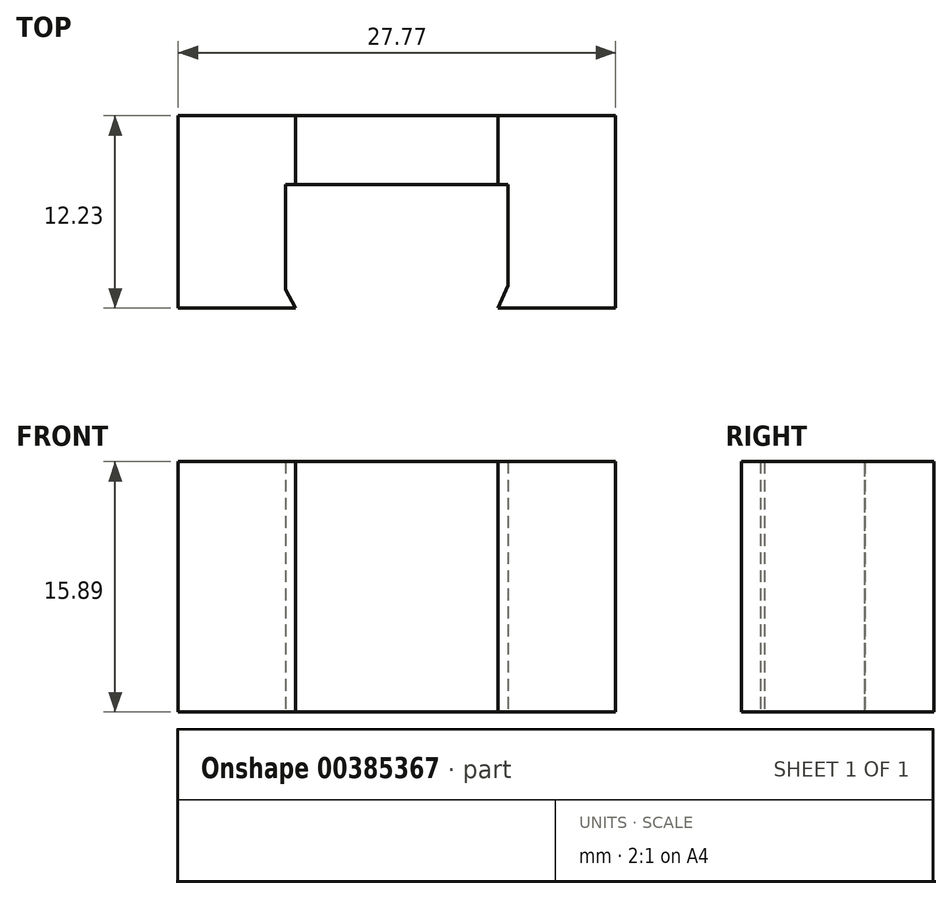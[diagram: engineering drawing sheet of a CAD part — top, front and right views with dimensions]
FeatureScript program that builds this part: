
annotation { "Feature Type Name" : "Feature", "Feature Type Description" : "" }
export const myFeature = defineFeature(function(context is Context, id is Id, definition is map)
    precondition{}
    {
        {
            var Q0;
            Q0=qCreatedBy(makeId("Front.planeOp"),FACE);
            var sketch = newSketch(context, id + "F0", { "sketchPlane" : qUnion([Q0])});
            skLineSegment(sketch, "E0", {"start": v(0, 0) * mm, "end": v(-27.77, 0) * mm});
            skLineSegment(sketch, "E1", {"start": v(-27.77, 0) * mm, "end": v(-27.77, -15.9) * mm});
            skLineSegment(sketch, "E2", {"start": v(-27.77, -15.9) * mm, "end": v(0, -15.9) * mm});
            skLineSegment(sketch, "E3", {"start": v(0, -15.9) * mm, "end": v(0, 0) * mm});
            skLineSegment(sketch, "E4", {"start": v(-20.32, 0) * mm, "end": v(-20.32, -15.9) * mm});
            skLineSegment(sketch, "E5", {"start": v(-20.32, -15.9) * mm, "end": v(-20.32, -11.79) * mm});
            skLineSegment(sketch, "E6", {"start": v(-7.45, -15.9) * mm, "end": v(-7.45, 0) * mm});
            skSolve(sketch);
        }
        {
            var Q0;
            {var subQ0=sQuery(id+"F0.wireOp",EDGE,"E3");Q0=makeQuery(id+"F0.imprint","IMPRINT",FACE,{"disambiguationData":[TD([[makeQuery(id+"F0.imprint","IMPRINT",EDGE,{"derivedFrom":subQ0}),1.0]])]});}
            var Q1;
            {var subQ1=sQuery(id+"F0.wireOp",EDGE,"E1");Q1=makeQuery(id+"F0.imprint","IMPRINT",FACE,{"disambiguationData":[TD([[makeQuery(id+"F0.imprint","IMPRINT",EDGE,{"derivedFrom":subQ1}),1.0]])]});}
            extrude(context, id + "F1", {"entities" : qUnion([Q0, Q1]), "depth" : 12.23 * mm});
        }
        {
            var Q0;
            {var subQ1=sQuery(id+"F0.wireOp",EDGE,"E4");Q0=makeQuery(id+"F0.imprint","IMPRINT",FACE,{"disambiguationData":[TD([[makeQuery(id+"F0.imprint","IMPRINT",EDGE,{"derivedFrom":subQ1}),1.0]])]});}
            extrude(context, id + "F2", {"entities" : qUnion([Q0]), "depth" : 4.39 * mm});
        }
        {
            var Q0;
            {var subQ0=sQuery(id+"F0.wireOp",EDGE,"E2");Q0=makeQuery(id+"F1.opExtrude","SWEPT_FACE",FACE,{"disambiguationData":[OSD([subQ0]),TDD([makeQuery(id+"F0.imprint","IMPRINT",EDGE,{"disambiguationData":[TD([[makeQuery(id+"F0.imprint","INTERSECT",VERTEX,{"derivedFrom":[subQ0,sQuery(id+"F0.wireOp",EDGE,"E3")]}),1.0]])],"derivedFrom":subQ0})])]});}
            var sketch = newSketch(context, id + "F3", { "sketchPlane" : qUnion([Q0])});
            skLineSegment(sketch, "E7", {"start": v(-7.45, 12.23) * mm, "end": v(-6.83, 10.78) * mm});
            skLineSegment(sketch, "E8", {"start": v(-6.83, 10.78) * mm, "end": v(-6.83, 4.42) * mm});
            skLineSegment(sketch, "E9", {"start": v(-6.83, 4.42) * mm, "end": v(-7.45, 4.42) * mm});
            skSolve(sketch);
        }
        {
            var Q0;
            {var subQ0=sQuery(id+"F3.wireOp",EDGE,"E7");Q0=makeQuery(id+"F3.imprint","IMPRINT",FACE,{"disambiguationData":[TD([[makeQuery(id+"F3.imprint","IMPRINT",EDGE,{"derivedFrom":subQ0}),-1.0]])]});}
            extrude(context, id + "F4", {"entities" : qUnion([Q0]), "operationType" : NewBodyOperationType.REMOVE, "oppositeDirection" : true, "depth" : 25.4 * mm});
        }
        {
            var Q0;
            {var subQ0=sQuery(id+"F0.wireOp",EDGE,"E2");Q0=makeQuery(id+"F1.opExtrude","SWEPT_FACE",FACE,{"disambiguationData":[OSD([subQ0]),TDD([makeQuery(id+"F0.imprint","IMPRINT",EDGE,{"disambiguationData":[TD([[makeQuery(id+"F0.imprint","INTERSECT",VERTEX,{"derivedFrom":[sQuery(id+"F0.wireOp",EDGE,"E1"),subQ0]}),-1.0]])],"derivedFrom":subQ0})])]});}
            var sketch = newSketch(context, id + "F5", { "sketchPlane" : qUnion([Q0])});
            skLineSegment(sketch, "E10", {"start": v(-20.32, 4.38) * mm, "end": v(-20.95, 4.38) * mm});
            skLineSegment(sketch, "E11", {"start": v(-20.95, 4.38) * mm, "end": v(-20.95, 11.04) * mm});
            skLineSegment(sketch, "E12", {"start": v(-20.95, 11.04) * mm, "end": v(-20.32, 12.23) * mm});
            skSolve(sketch);
        }
        {
            var Q0;
            {var subQ0=sQuery(id+"F5.wireOp",EDGE,"E10");Q0=makeQuery(id+"F5.imprint","IMPRINT",FACE,{"disambiguationData":[TD([[makeQuery(id+"F5.imprint","IMPRINT",EDGE,{"derivedFrom":subQ0}),-1.0]])]});}
            extrude(context, id + "F6", {"entities" : qUnion([Q0]), "operationType" : NewBodyOperationType.REMOVE, "oppositeDirection" : true, "depth" : 25.4 * mm});
        }
        {
            var Q0;
            {var subQ0=sQuery(id+"F0.wireOp",EDGE,"E2");Q0=makeQuery(id+"F1.opExtrude","SWEPT_FACE",FACE,{"disambiguationData":[OSD([subQ0]),TDD([makeQuery(id+"F0.imprint","IMPRINT",EDGE,{"disambiguationData":[TD([[makeQuery(id+"F0.imprint","INTERSECT",VERTEX,{"derivedFrom":[subQ0,sQuery(id+"F0.wireOp",EDGE,"E3")]}),1.0]])],"derivedFrom":subQ0})])]});}
            var sketch = newSketch(context, id + "F7", { "sketchPlane" : qUnion([Q0])});
            skLineSegment(sketch, "E13", {"start": v(-7.45, 4.42) * mm, "end": v(-7.45, 4.4) * mm});
            skLineSegment(sketch, "E14", {"start": v(-7.45, 4.4) * mm, "end": v(-6.83, 4.4) * mm});
            skLineSegment(sketch, "E15", {"start": v(-6.83, 4.4) * mm, "end": v(-6.83, 4.42) * mm});
            skLineSegment(sketch, "E16", {"start": v(-7.45, 4.42) * mm, "end": v(-6.83, 4.42) * mm});
            skSolve(sketch);
        }
        {
            var Q0;
            Q0 = qSketchRegion(id + "F7", true);
            extrude(context, id + "F8", {"entities" : qUnion([Q0]), "operationType" : NewBodyOperationType.REMOVE, "endBound" : BoundingType.THROUGH_ALL, "oppositeDirection" : true, "depth" : 25.4 * mm});
        }
    });
